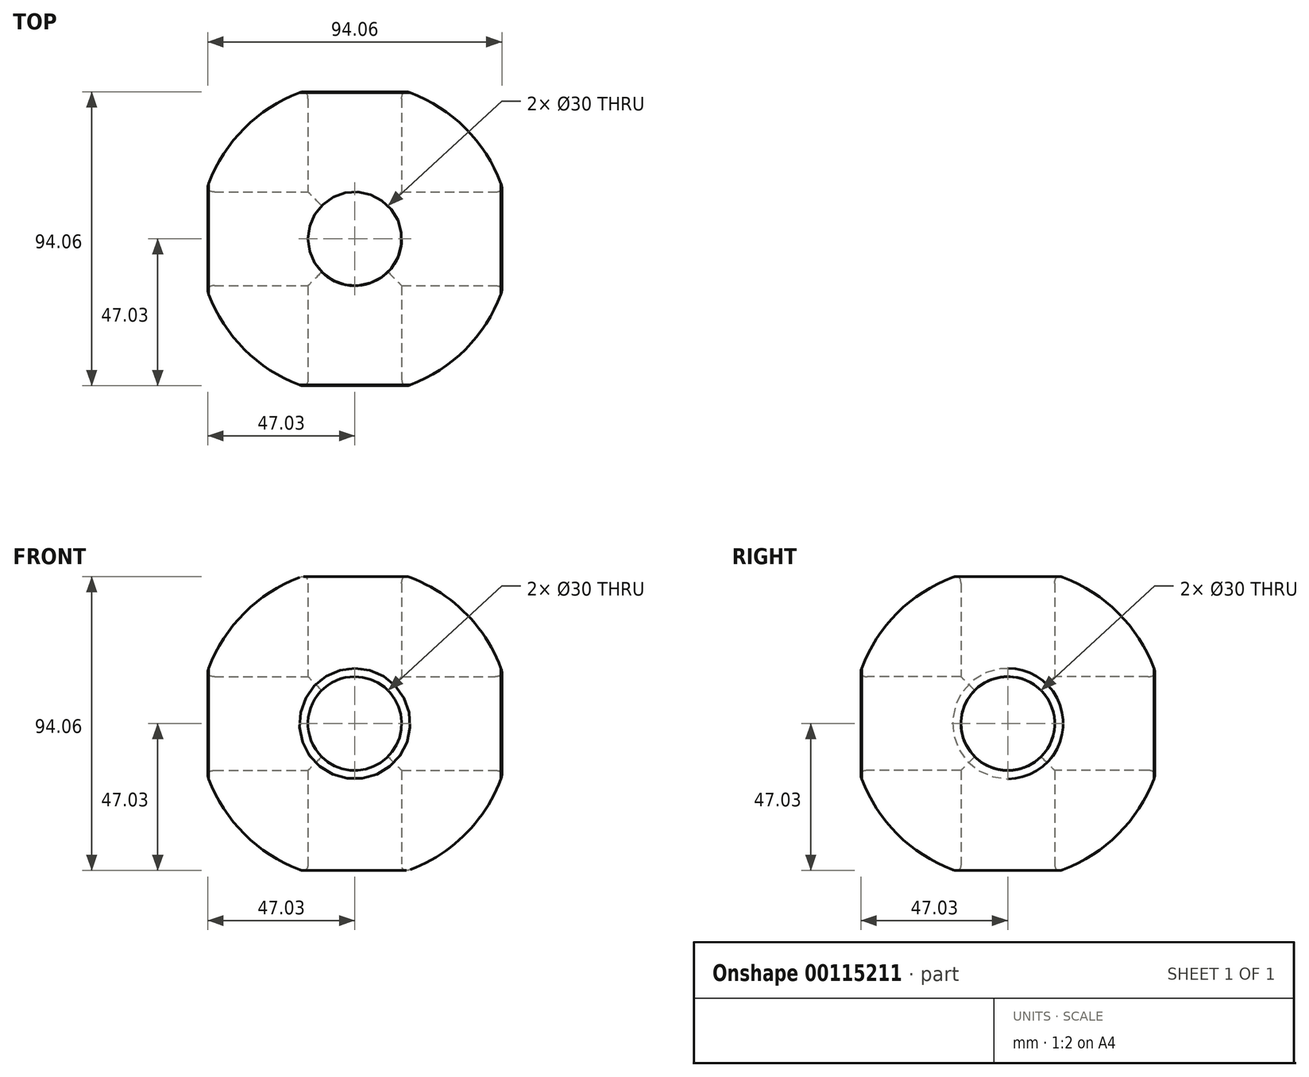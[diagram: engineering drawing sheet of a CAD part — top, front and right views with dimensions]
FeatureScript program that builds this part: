
annotation { "Feature Type Name" : "Feature", "Feature Type Description" : "" }
export const myFeature = defineFeature(function(context is Context, id is Id, definition is map)
    precondition{}
    {
        {
            var Q0;
            Q0=qCreatedBy(makeId("Front.planeOp"),FACE);
            var sketch = newSketch(context, id + "F0", { "sketchPlane" : qUnion([Q0])});
            skLineSegment(sketch, "E0", {"start": v(0, -50) * mm, "end": v(0, 50) * mm});
            skArc(sketch, "E1", {"start": v(0, 50) * mm, "mid": v(-50, 0) * mm, "end": v(0, -50) * mm});
            skSolve(sketch);
        }
        {
            var Q0;
            Q0 = qSketchRegion(id + "F0", true);
            var Q1;
            Q1=sQuery(id+"F0.wireOp",EDGE,"E0");
            revolve(context, id + "F1", {"entities" : qUnion([Q0]), "axis" : qUnion([Q1]), "revolveType" : RevolveType.FULL});
        }
        {
            var Q0;
            Q0=qCreatedBy(makeId("Top.planeOp"),FACE);
            var sketch = newSketch(context, id + "F2", { "sketchPlane" : qUnion([Q0])});
            skCircle(sketch, "E2", {"center": v(0, 0) * mm, "radius": 15 * mm});
            skSolve(sketch);
        }
        {
            var Q0;
            Q0 = qSketchRegion(id + "F2", true);
            extrude(context, id + "F3", {"entities" : qUnion([Q0]), "operationType" : NewBodyOperationType.REMOVE, "endBound" : BoundingType.THROUGH_ALL, "depth" : 25 * mm, "hasSecondDirection" : true, "secondDirectionBound" : SecondDirectionBoundingType.THROUGH_ALL, "secondDirectionOppositeDirection" : true, "secondDirectionDepth" : 25 * mm});
        }
        {
            var Q0;
            Q0=qCreatedBy(makeId("Front.planeOp"),FACE);
            var sketch = newSketch(context, id + "F4", { "sketchPlane" : qUnion([Q0])});
            skCircle(sketch, "E3", {"center": v(0, 0) * mm, "radius": 15 * mm});
            skSolve(sketch);
        }
        {
            var Q0;
            Q0 = qSketchRegion(id + "F4", true);
            extrude(context, id + "F5", {"entities" : qUnion([Q0]), "operationType" : NewBodyOperationType.REMOVE, "endBound" : BoundingType.THROUGH_ALL, "oppositeDirection" : true, "depth" : 25 * mm, "hasSecondDirection" : true, "secondDirectionBound" : SecondDirectionBoundingType.THROUGH_ALL, "secondDirectionOppositeDirection" : false, "secondDirectionDepth" : 25 * mm});
        }
        {
            var Q0;
            Q0=qCreatedBy(makeId("Right.planeOp"),FACE);
            var sketch = newSketch(context, id + "F6", { "sketchPlane" : qUnion([Q0])});
            skCircle(sketch, "E4", {"center": v(0, 0) * mm, "radius": 15 * mm});
            skSolve(sketch);
        }
        {
            var Q0;
            Q0 = qSketchRegion(id + "F6", true);
            extrude(context, id + "F7", {"entities" : qUnion([Q0]), "operationType" : NewBodyOperationType.REMOVE, "endBound" : BoundingType.THROUGH_ALL, "oppositeDirection" : true, "depth" : 25 * mm, "hasSecondDirection" : true, "secondDirectionBound" : SecondDirectionBoundingType.THROUGH_ALL, "secondDirectionOppositeDirection" : false, "secondDirectionDepth" : 25 * mm});
        }
        {
            var Q0;
            Q0=makeQuery(id+"F3.boolean.opBoolean","INTERSECT",EDGE,{"disambiguationData":[OD(1.0)],"derivedFrom":[makeQuery(id+"F1.opRevolve","SWEPT_FACE",FACE,{"disambiguationData":[OSD([sQuery(id+"F0.wireOp",EDGE,"E1")])]}),makeQuery(id+"F3.opExtrude","SWEPT_FACE",FACE,{"disambiguationData":[OSD([sQuery(id+"F2.wireOp",EDGE,"E2")])]})]});
            var Q1;
            Q1=makeQuery(id+"F5.boolean.opBoolean","INTERSECT",EDGE,{"disambiguationData":[OD(0.0)],"derivedFrom":[makeQuery(id+"F1.opRevolve","SWEPT_FACE",FACE,{"disambiguationData":[OSD([sQuery(id+"F0.wireOp",EDGE,"E1")])]}),makeQuery(id+"F5.opExtrude","SWEPT_FACE",FACE,{"disambiguationData":[OSD([sQuery(id+"F4.wireOp",EDGE,"E3")])]})]});
            var Q2;
            Q2=makeQuery(id+"F7.boolean.opBoolean","INTERSECT",EDGE,{"disambiguationData":[OD(1.0)],"derivedFrom":[makeQuery(id+"F1.opRevolve","SWEPT_FACE",FACE,{"disambiguationData":[OSD([sQuery(id+"F0.wireOp",EDGE,"E1")])]}),makeQuery(id+"F7.opExtrude","SWEPT_FACE",FACE,{"disambiguationData":[OSD([sQuery(id+"F6.wireOp",EDGE,"E4")])]})]});
            var Q3;
            Q3=makeQuery(id+"F5.boolean.opBoolean","INTERSECT",EDGE,{"disambiguationData":[OD(1.0)],"derivedFrom":[makeQuery(id+"F1.opRevolve","SWEPT_FACE",FACE,{"disambiguationData":[OSD([sQuery(id+"F0.wireOp",EDGE,"E1")])]}),makeQuery(id+"F5.opExtrude","SWEPT_FACE",FACE,{"disambiguationData":[OSD([sQuery(id+"F4.wireOp",EDGE,"E3")])]})]});
            var Q4;
            Q4=makeQuery(id+"F7.boolean.opBoolean","INTERSECT",EDGE,{"disambiguationData":[OD(0.0)],"derivedFrom":[makeQuery(id+"F1.opRevolve","SWEPT_FACE",FACE,{"disambiguationData":[OSD([sQuery(id+"F0.wireOp",EDGE,"E1")])]}),makeQuery(id+"F7.opExtrude","SWEPT_FACE",FACE,{"disambiguationData":[OSD([sQuery(id+"F6.wireOp",EDGE,"E4")])]})]});
            var Q5;
            Q5=makeQuery(id+"F3.boolean.opBoolean","INTERSECT",EDGE,{"disambiguationData":[OD(0.0)],"derivedFrom":[makeQuery(id+"F1.opRevolve","SWEPT_FACE",FACE,{"disambiguationData":[OSD([sQuery(id+"F0.wireOp",EDGE,"E1")])]}),makeQuery(id+"F3.opExtrude","SWEPT_FACE",FACE,{"disambiguationData":[OSD([sQuery(id+"F2.wireOp",EDGE,"E2")])]})]});
            fillet(context, id + "F8", {"entities" : qUnion([Q0, Q1, Q2, Q3, Q4, Q5]), "radius" : 2 * mm, "tangentPropagation" : true, "rho" : 0.5, "crossSection" : FilletCrossSection.CONIC, "allowEdgeOverflow" : false});
        }
    });
